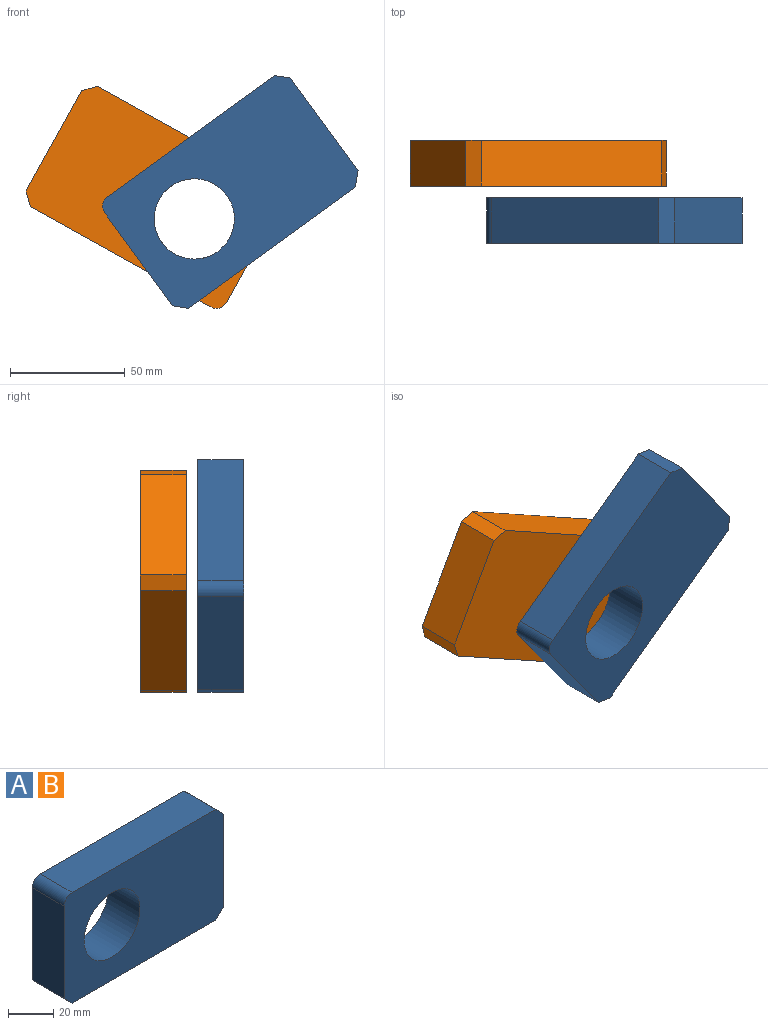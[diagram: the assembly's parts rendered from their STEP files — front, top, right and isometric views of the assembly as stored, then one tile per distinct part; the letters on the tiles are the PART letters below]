
ASSEMBLY  parts=2 mates=2
PART A: 11 faces, bbox 100x20x60 mm
  f0: plane 90x20mm, normal (0,0,1), area 1800mm2, adj f5,f6,f7,f10
  f1: plane 50x20mm, normal (-1,0,0), area 1000mm2, adj f5,f6,f7,f9
  f2: plane 90x20mm, normal (0,0,-1), area 1800mm2, adj f5,f6,f8,f9
  f3: cylinder r=17.5mm len=35mm, axis (0,1,0), area 2199.1mm2, adj f5,f6
  f4: plane 50x20mm, normal (1,0,0), area 1000mm2, adj f5,f6,f8,f10
  f5: plane 100x60mm, normal (0,-1,0), area 4995mm2, adj f0,f1,f2,f3,f4,f7,f8,f9
  f6: plane 100x60mm, normal (0,1,0), area 4995mm2, adj f0,f1,f2,f3,f4,f7,f8,f9
  f7: cylinder r=5mm len=20mm, axis (0,1,0), area 157.1mm2, adj f0,f1,f5,f6
  f8: plane 20x5mm, normal (0.71,0,-0.71), area 141.4mm2, adj f2,f4,f5,f6
  f9: plane 20x5mm, normal (-0.71,0,-0.71), area 141.4mm2, adj f1,f2,f5,f6
  f10: plane 20x5mm, normal (0.71,0,0.71), area 141.4mm2, adj f0,f4,f5,f6
PART B: same geometry as A
PLACE A rot(axis=(0,-1,0),36deg) t=(20.63,-87.23,-176.72)mm
PLACE B rot(axis=(0,-1,0),150.9deg) t=(68.08,-62.23,-123.18)mm
MATE cylindrical A.f3 <-> B.f3  axis (0,1,0) through (27.28,-107.23,-134.82)mm
MATE planar A.f6 <-> B.f3  axis (0,1,0) through (46.5,-87.23,-120.81)mm
